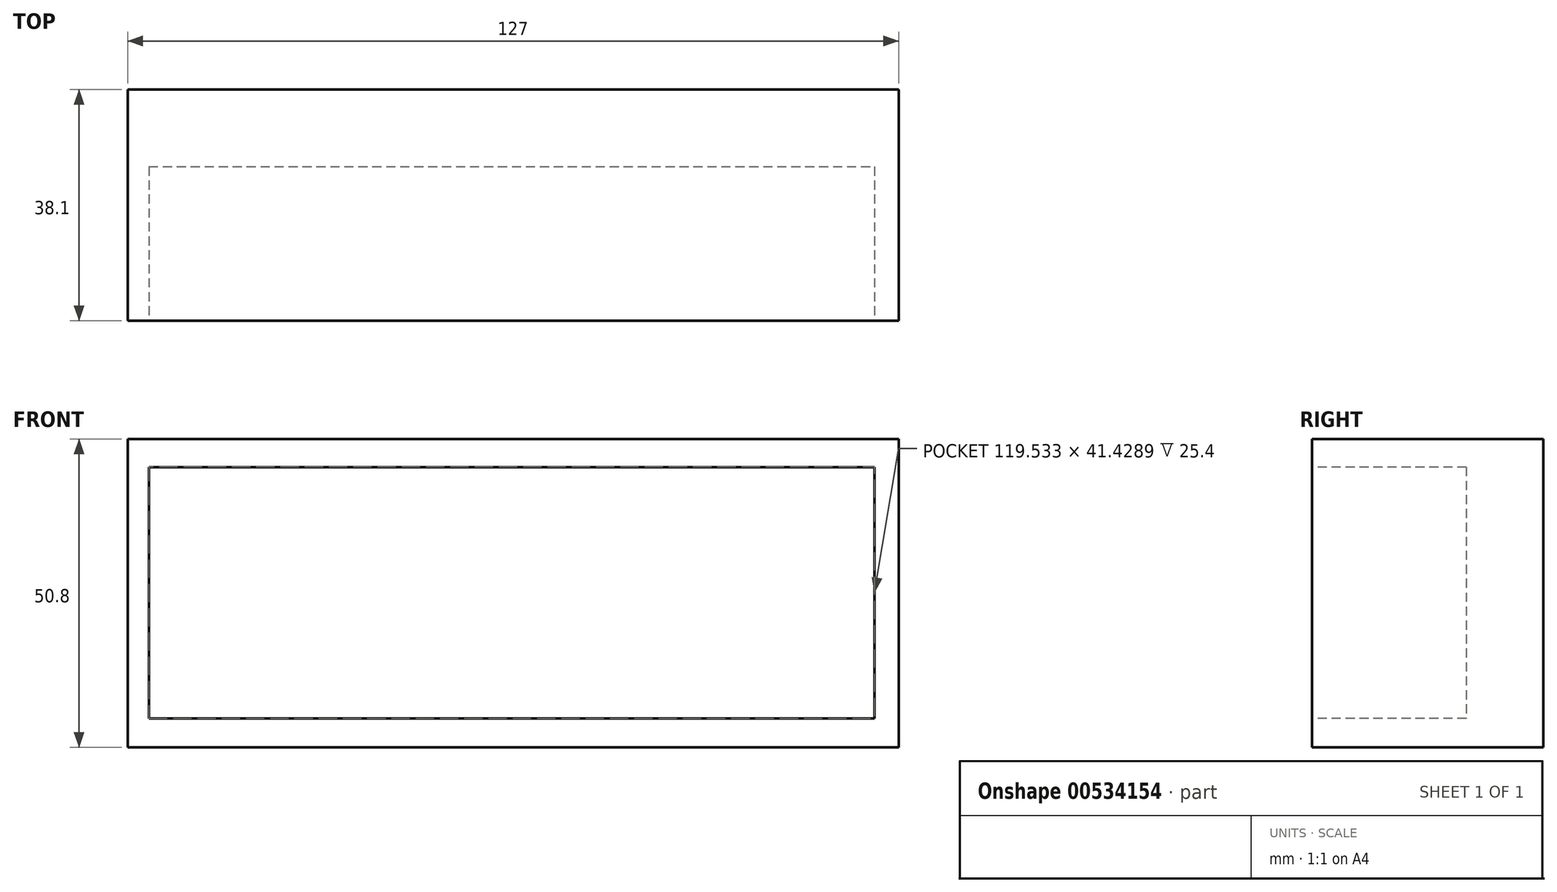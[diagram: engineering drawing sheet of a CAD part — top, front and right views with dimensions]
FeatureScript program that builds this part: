
annotation { "Feature Type Name" : "Feature", "Feature Type Description" : "" }
export const myFeature = defineFeature(function(context is Context, id is Id, definition is map)
    precondition{}
    {
        {
            var Q0;
            Q0=qCreatedBy(makeId("Front.planeOp"),FACE);
            var sketch = newSketch(context, id + "F0", { "sketchPlane" : qUnion([Q0])});
            skLineSegment(sketch, "E0.bottom", {"start": v(-64.7, 62) * mm, "end": v(62.3, 62) * mm});
            skLineSegment(sketch, "E0.top", {"start": v(-64.7, 11.2) * mm, "end": v(62.3, 11.2) * mm});
            skLineSegment(sketch, "E0.left", {"start": v(-64.7, 62) * mm, "end": v(-64.7, 11.2) * mm});
            skLineSegment(sketch, "E0.right", {"start": v(62.3, 62) * mm, "end": v(62.3, 11.2) * mm});
            skSolve(sketch);
        }
        {
            var Q0;
            Q0=makeQuery(id+"F0.imprint","IMPRINT",FACE,{"disambiguationData":[TD([[makeQuery(id+"F0.imprint","IMPRINT",EDGE,{"derivedFrom":sQuery(id+"F0.wireOp",EDGE,"E0.bottom")}),-1.0]])]});
            extrude(context, id + "F1", {"entities" : qUnion([Q0]), "depth" : 38.1 * mm, "offsetDistance" : 25.4 * mm});
        }
        {
            var Q0;
            Q0=makeQuery(id+"F1.opExtrude","CAP_FACE",FACE,{"disambiguationData":[OSD([sQuery(id+"F0.wireOp",EDGE,"E0.bottom"),sQuery(id+"F0.wireOp",EDGE,"E0.top"),sQuery(id+"F0.wireOp",EDGE,"E0.left"),sQuery(id+"F0.wireOp",EDGE,"E0.right")])],"isStart":false});
            var sketch = newSketch(context, id + "F2", { "sketchPlane" : qUnion([Q0])});
            skLineSegment(sketch, "E1.bottom", {"start": v(-61.2, 57.4) * mm, "end": v(58.33, 57.4) * mm});
            skLineSegment(sketch, "E1.top", {"start": v(-61.2, 15.96) * mm, "end": v(58.33, 15.96) * mm});
            skLineSegment(sketch, "E1.left", {"start": v(-61.2, 57.4) * mm, "end": v(-61.2, 15.96) * mm});
            skLineSegment(sketch, "E1.right", {"start": v(58.33, 57.4) * mm, "end": v(58.33, 15.96) * mm});
            skSolve(sketch);
        }
        {
            var Q0;
            Q0=makeQuery(id+"F2.imprint","IMPRINT",FACE,{"disambiguationData":[TD([[makeQuery(id+"F2.imprint","IMPRINT",EDGE,{"derivedFrom":sQuery(id+"F2.wireOp",EDGE,"E1.bottom")}),-1.0]])]});
            extrude(context, id + "F3", {"entities" : qUnion([Q0]), "operationType" : NewBodyOperationType.REMOVE, "oppositeDirection" : true, "depth" : 25.4 * mm, "offsetDistance" : 25.4 * mm});
        }
    });
